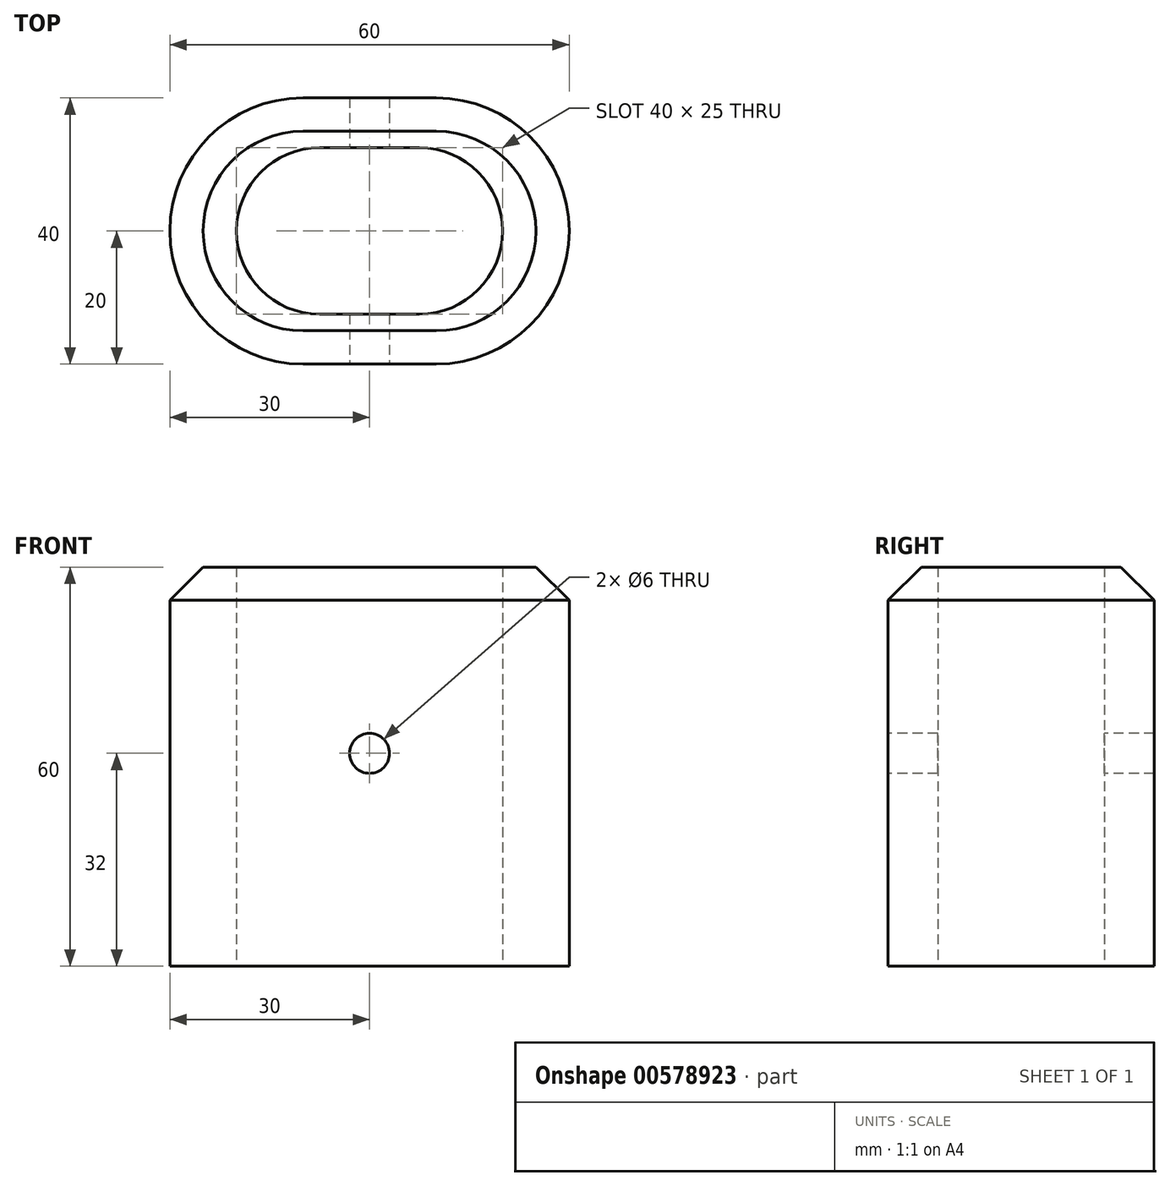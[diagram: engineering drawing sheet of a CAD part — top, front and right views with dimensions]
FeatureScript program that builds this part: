
annotation { "Feature Type Name" : "Feature", "Feature Type Description" : "" }
export const myFeature = defineFeature(function(context is Context, id is Id, definition is map)
    precondition{}
    {
        {
            var Q0;
            Q0=qCreatedBy(makeId("Top.planeOp"),FACE);
            var sketch = newSketch(context, id + "F0", { "sketchPlane" : qUnion([Q0])});
            skLineSegment(sketch, "E0.bottom", {"start": v(10, 20) * mm, "end": v(-10, 20) * mm});
            skLineSegment(sketch, "E0.top", {"start": v(10, -20) * mm, "end": v(-10, -20) * mm});
            skLineSegment(sketch, "E0.left", {"start": v(30, 0) * mm, "end": v(30, 0) * mm});
            skLineSegment(sketch, "E0.right", {"start": v(-30, 0) * mm, "end": v(-30, 0) * mm});
            skPoint(sketch, "E0.middle", {"position": v(0, 0) * mm});
            skPoint(sketch, "E1.visualSharp", {"position": v(30, 20) * mm});
            skArc(sketch, "E1.filletArc", {"start": v(30, 0) * mm, "mid": v(24.14, 14.14) * mm, "end": v(10, 20) * mm});
            skPoint(sketch, "E2.visualSharp", {"position": v(-30, 20) * mm});
            skArc(sketch, "E2.filletArc", {"start": v(-10, 20) * mm, "mid": v(-24.14, 14.14) * mm, "end": v(-30, 0) * mm});
            skPoint(sketch, "E3.visualSharp", {"position": v(-30, -20) * mm});
            skArc(sketch, "E3.filletArc", {"start": v(-30, 0) * mm, "mid": v(-24.14, -14.14) * mm, "end": v(-10, -20) * mm});
            skPoint(sketch, "E4.visualSharp", {"position": v(30, -20) * mm});
            skArc(sketch, "E4.filletArc", {"start": v(10, -20) * mm, "mid": v(24.14, -14.14) * mm, "end": v(30, 0) * mm});
            skLineSegment(sketch, "E5.bottom", {"start": v(7.5, 12.5) * mm, "end": v(-7.5, 12.5) * mm});
            skLineSegment(sketch, "E5.top", {"start": v(7.5, -12.5) * mm, "end": v(-7.5, -12.5) * mm});
            skLineSegment(sketch, "E5.left", {"start": v(20, 0) * mm, "end": v(20, 0) * mm});
            skLineSegment(sketch, "E5.right", {"start": v(-20, 0) * mm, "end": v(-20, 0) * mm});
            skPoint(sketch, "E6.visualSharp", {"position": v(20, 12.5) * mm});
            skArc(sketch, "E6.filletArc", {"start": v(20, 0) * mm, "mid": v(16.34, 8.84) * mm, "end": v(7.5, 12.5) * mm});
            skPoint(sketch, "E7.visualSharp", {"position": v(-20, 12.5) * mm});
            skArc(sketch, "E7.filletArc", {"start": v(-7.5, 12.5) * mm, "mid": v(-16.34, 8.84) * mm, "end": v(-20, 0) * mm});
            skPoint(sketch, "E8.visualSharp", {"position": v(20, -12.5) * mm});
            skArc(sketch, "E8.filletArc", {"start": v(7.5, -12.5) * mm, "mid": v(16.34, -8.84) * mm, "end": v(20, 0) * mm});
            skPoint(sketch, "E9.visualSharp", {"position": v(-20, -12.5) * mm});
            skArc(sketch, "E9.filletArc", {"start": v(-20, 0) * mm, "mid": v(-16.34, -8.84) * mm, "end": v(-7.5, -12.5) * mm});
            skSolve(sketch);
        }
        {
            var Q0;
            Q0=makeQuery(id+"F0.imprint","IMPRINT",FACE,{"disambiguationData":[TD([[makeQuery(id+"F0.imprint","IMPRINT",EDGE,{"derivedFrom":sQuery(id+"F0.wireOp",EDGE,"E0.bottom")}),1.0]])]});
            extrude(context, id + "F1", {"entities" : qUnion([Q0]), "depth" : 60 * mm, "offsetDistance" : 25 * mm});
        }
        {
            var Q0;
            Q0=makeQuery(id+"F1.opExtrude","CAP_EDGE",EDGE,{"disambiguationData":[OSD([sQuery(id+"F0.wireOp",EDGE,"E1.filletArc"),sQuery(id+"F0.wireOp",EDGE,"E4.filletArc")])],"isStart":false});
            chamfer(context, id + "F2", {"entities" : qUnion([Q0]), "width" : 5 * mm, "tangentPropagation" : true});
        }
        {
            var Q0;
            Q0=makeQuery(id+"F1.opExtrude","SWEPT_FACE",FACE,{"disambiguationData":[OSD([sQuery(id+"F0.wireOp",EDGE,"E0.top")])]});
            var sketch = newSketch(context, id + "F3", { "sketchPlane" : qUnion([Q0])});
            skCircle(sketch, "E10", {"center": v(0, 32) * mm, "radius": 3 * mm});
            skSolve(sketch);
        }
        {
            var Q0;
            Q0 = qSketchRegion(id + "F3", true);
            extrude(context, id + "F4", {"entities" : qUnion([Q0]), "operationType" : NewBodyOperationType.REMOVE, "endBound" : BoundingType.THROUGH_ALL, "oppositeDirection" : true, "depth" : 25 * mm, "offsetDistance" : 25 * mm});
        }
    });
